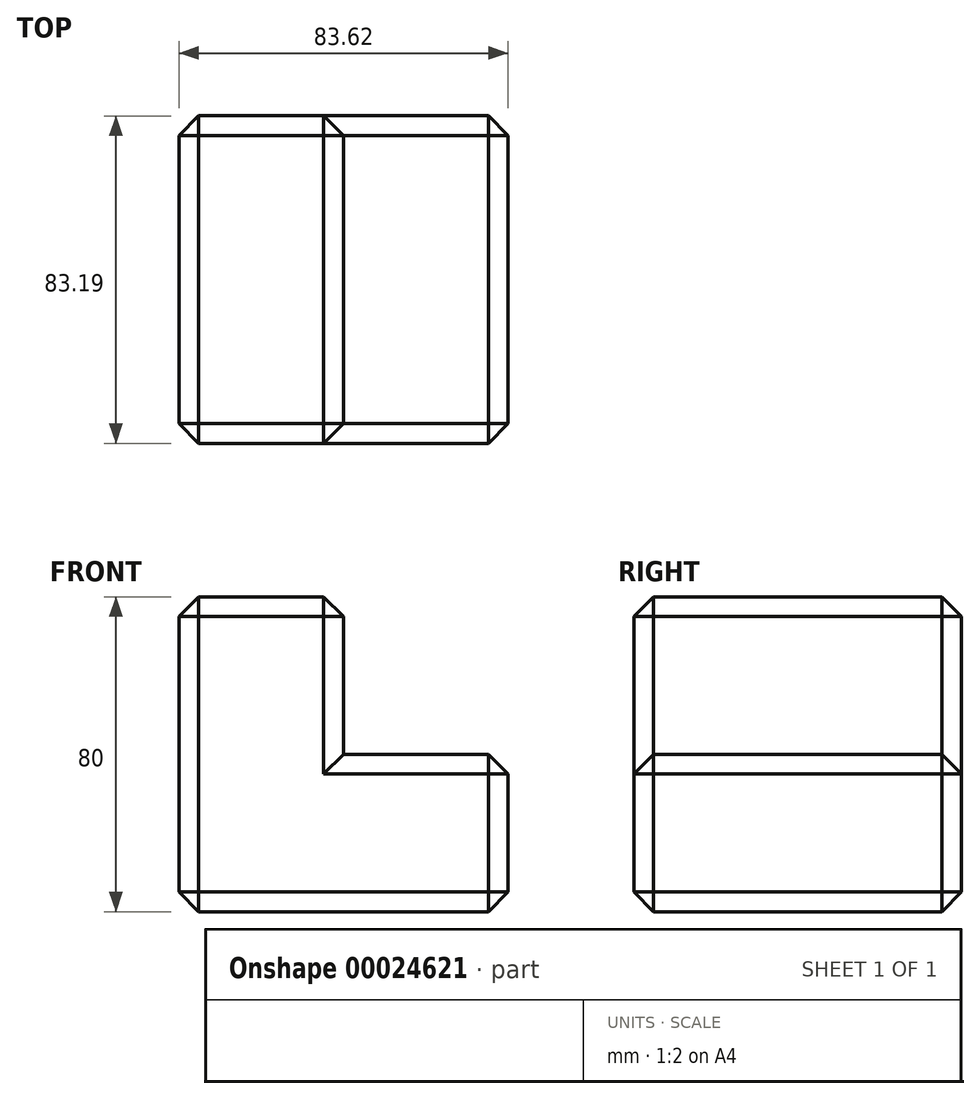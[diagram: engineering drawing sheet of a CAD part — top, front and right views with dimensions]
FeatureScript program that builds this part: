
annotation { "Feature Type Name" : "Feature", "Feature Type Description" : "" }
export const myFeature = defineFeature(function(context is Context, id is Id, definition is map)
    precondition{}
    {
        {
            var Q0;
            Q0=qCreatedBy(makeId("Top.planeOp"),FACE);
            var sketch = newSketch(context, id + "F0", { "sketchPlane" : qUnion([Q0])});
            skLineSegment(sketch, "E0.bottom", {"start": v(-59.13, -45.93) * mm, "end": v(24.5, -45.93) * mm});
            skLineSegment(sketch, "E0.top", {"start": v(-59.13, 37.26) * mm, "end": v(24.5, 37.26) * mm});
            skLineSegment(sketch, "E0.left", {"start": v(-59.13, -45.93) * mm, "end": v(-59.13, 37.26) * mm});
            skLineSegment(sketch, "E0.right", {"start": v(24.5, -45.93) * mm, "end": v(24.5, 37.26) * mm});
            skSolve(sketch);
        }
        {
            var Q0;
            Q0=makeQuery(id+"F0.imprint","IMPRINT",FACE,{"disambiguationData":[TD([[makeQuery(id+"F0.imprint","IMPRINT",EDGE,{"derivedFrom":sQuery(id+"F0.wireOp",EDGE,"E0.bottom")}),1.0]])]});
            extrude(context, id + "F1", {"entities" : qUnion([Q0]), "depth" : 40 * mm});
        }
        {
            var Q0;
            Q0=makeQuery(id+"F1.opExtrude","CAP_FACE",FACE,{"disambiguationData":[OSD([sQuery(id+"F0.wireOp",EDGE,"E0.bottom"),sQuery(id+"F0.wireOp",EDGE,"E0.top"),sQuery(id+"F0.wireOp",EDGE,"E0.left"),sQuery(id+"F0.wireOp",EDGE,"E0.right")])],"isStart":false});
            var sketch = newSketch(context, id + "F2", { "sketchPlane" : qUnion([Q0])});
            skLineSegment(sketch, "E1", {"start": v(-17.32, 37.26) * mm, "end": v(-17.32, -45.93) * mm});
            skSolve(sketch);
        }
        {
            var Q0;
            {var subQ1=sQuery(id+"F2.wireOp",EDGE,"E1");Q0=makeQuery(id+"F2.imprint","IMPRINT",FACE,{"disambiguationData":[TD([[makeQuery(id+"F2.imprint","IMPRINT",EDGE,{"derivedFrom":subQ1}),-1.0]])]});}
            extrude(context, id + "F3", {"entities" : qUnion([Q0]), "operationType" : NewBodyOperationType.ADD, "depth" : 40 * mm});
        }
        {
            var Q0;
            Q0=makeQuery(id+"F3.opExtrude","CAP_EDGE",EDGE,{"disambiguationData":[OSD([sQuery(id+"F0.wireOp",EDGE,"E0.bottom")])],"isStart":false});
            var Q1;
            Q1=makeQuery(id+"F3.opExtrude","CAP_EDGE",EDGE,{"disambiguationData":[OSD([sQuery(id+"F2.wireOp",EDGE,"E1")])],"isStart":false});
            var Q2;
            Q2=makeQuery(id+"F3.opExtrude","SWEPT_EDGE",EDGE,{"disambiguationData":[OSD([sQuery(id+"F0.wireOp",EDGE,"E0.bottom"),sQuery(id+"F2.wireOp",EDGE,"E1")])]});
            var Q3;
            Q3=makeQuery(id+"F3.opExtrude","CAP_EDGE",EDGE,{"disambiguationData":[OSD([sQuery(id+"F2.wireOp",EDGE,"E1")])],"isStart":true});
            var Q4;
            Q4=makeQuery(id+"F1.opExtrude","CAP_EDGE",EDGE,{"disambiguationData":[OSD([sQuery(id+"F0.wireOp",EDGE,"E0.bottom")])],"isStart":false});
            var Q5;
            Q5=makeQuery(id+"F1.opExtrude","CAP_EDGE",EDGE,{"disambiguationData":[OSD([sQuery(id+"F0.wireOp",EDGE,"E0.right")])],"isStart":false});
            var Q6;
            Q6=makeQuery(id+"F1.opExtrude","SWEPT_EDGE",EDGE,{"disambiguationData":[OSD([sQuery(id+"F0.wireOp",EDGE,"E0.bottom"),sQuery(id+"F0.wireOp",EDGE,"E0.right")])]});
            var Q7;
            Q7=makeQuery(id+"F1.opExtrude","SWEPT_FACE",FACE,{"disambiguationData":[OSD([sQuery(id+"F0.wireOp",EDGE,"E0.right")])]});
            var Q8;
            {var subQ0=sQuery(id+"F0.wireOp",EDGE,"E0.bottom");Q8=makeQuery(id+"F3.boolean.opBoolean","MERGE",FACE,{"derivedFrom":[makeQuery(id+"F1.opExtrude","SWEPT_FACE",FACE,{"disambiguationData":[OSD([subQ0])]}),makeQuery(id+"F3.opExtrude","SWEPT_FACE",FACE,{"disambiguationData":[OSD([subQ0])]})]});}
            var Q9;
            Q9=makeQuery(id+"F3.opExtrude","CAP_FACE",FACE,{"disambiguationData":[OSD([sQuery(id+"F0.wireOp",EDGE,"E0.bottom"),sQuery(id+"F0.wireOp",EDGE,"E0.top"),sQuery(id+"F0.wireOp",EDGE,"E0.left"),sQuery(id+"F2.wireOp",EDGE,"E1")])],"isStart":false});
            var Q10;
            {var subQ0=sQuery(id+"F0.wireOp",EDGE,"E0.left");Q10=makeQuery(id+"F3.boolean.opBoolean","MERGE",FACE,{"derivedFrom":[makeQuery(id+"F1.opExtrude","SWEPT_FACE",FACE,{"disambiguationData":[OSD([subQ0])]}),makeQuery(id+"F3.opExtrude","SWEPT_FACE",FACE,{"disambiguationData":[OSD([subQ0])]})]});}
            var Q11;
            {var subQ0=sQuery(id+"F0.wireOp",EDGE,"E0.top");Q11=makeQuery(id+"F3.boolean.opBoolean","MERGE",FACE,{"derivedFrom":[makeQuery(id+"F1.opExtrude","SWEPT_FACE",FACE,{"disambiguationData":[OSD([subQ0])]}),makeQuery(id+"F3.opExtrude","SWEPT_FACE",FACE,{"disambiguationData":[OSD([subQ0])]})]});}
            var Q12;
            Q12=makeQuery(id+"F1.opExtrude","CAP_FACE",FACE,{"disambiguationData":[OSD([sQuery(id+"F0.wireOp",EDGE,"E0.bottom"),sQuery(id+"F0.wireOp",EDGE,"E0.top"),sQuery(id+"F0.wireOp",EDGE,"E0.left"),sQuery(id+"F0.wireOp",EDGE,"E0.right")])],"isStart":true});
            chamfer(context, id + "F4", {"entities" : qUnion([Q0, Q1, Q2, Q3, Q4, Q5, Q6, Q7, Q8, Q9, Q10, Q11, Q12]), "width" : 5 * mm, "tangentPropagation" : true});
        }
    });
